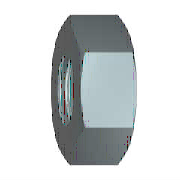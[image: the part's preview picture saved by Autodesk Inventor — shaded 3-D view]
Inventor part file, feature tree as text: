
AUTODESK INVENTOR PART (.ipt)
format: ipt  version: 2018 (Build 220112000, 112)  size: 173,568 bytes
history: native  units: mm (DEFAULTED — no unit token found)
features: sketch x3, chamfer x1, hole x1, other x1, plane x1
ambient origin geometry x7: Origin, YZ Plane, XZ Plane, X Axis, Y Axis, Z Axis, Center Point
bodies: Solid1 (feature_tree), Body (feature_tree)
feature tree (7):
  chamfer  "Chamfer1"  Distance=4.363323mm
  hole  "Thread"  [1 undecoded]
  other  "Work Axis1"
  plane  "Work Plane1"
  sketch  "Sketch1"  dims[d0=8.082904mm]
  sketch  "Sketch2"  dims[d1=3.2mm]
  sketch  "Sketch3"  dims[d2=0.0mm d3=4.363323mm d4=4.363323mm d5=7.0mm d6=7.0mm d7=90.0deg d25=3.242mm d26=6.0mm d27=4.0mm d28=2.0mm d29=14.3117mm d30=8.0mm d31=20.594885mm d8=0.378886mm d9=30.0deg d10=0.378886mm d11=30.0deg d13=0.0mm d14=0.0mm d39=0.0mm d40=0.378886mm d41=0.378886mm d42=0.0mm]
note: 1 required parameter value undecoded (feature->parameter linkage not recoverable at this tier; creation-order binding heuristic only, values carry confidence <= 0.55)
